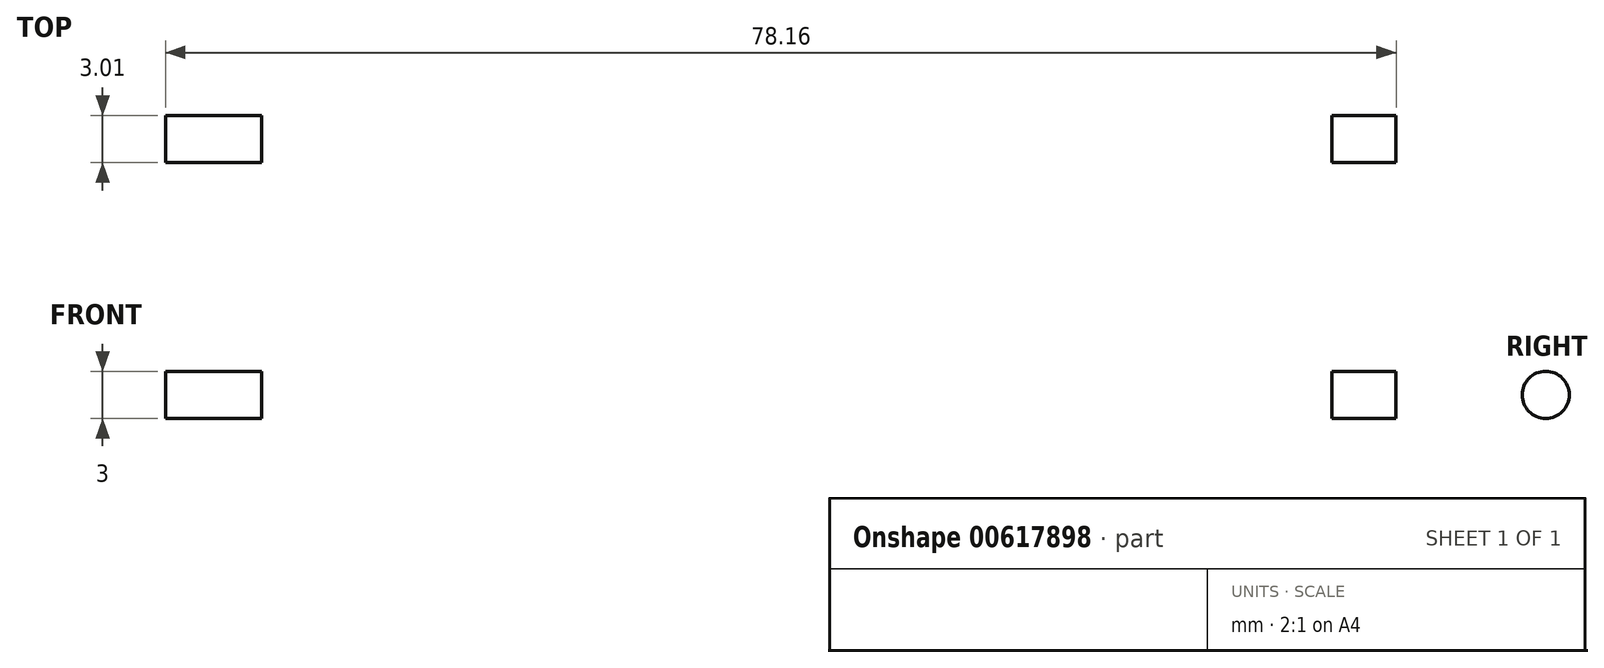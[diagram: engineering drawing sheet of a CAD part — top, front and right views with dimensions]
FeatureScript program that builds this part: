
annotation { "Feature Type Name" : "Feature", "Feature Type Description" : "" }
export const myFeature = defineFeature(function(context is Context, id is Id, definition is map)
    precondition{}
    {
        {
            var Q0;
            Q0=qCreatedBy(makeId("Front.planeOp"),FACE);
            var sketch = newSketch(context, id + "F0", { "sketchPlane" : qUnion([Q0])});
            skLineSegment(sketch, "E0.bottom", {"start": v(-39.07, 21.55) * mm, "end": v(39.08, 21.55) * mm});
            skLineSegment(sketch, "E0.top", {"start": v(-39.08, -21.55) * mm, "end": v(39.08, -21.55) * mm});
            skLineSegment(sketch, "E0.left", {"start": v(-39.07, 21.55) * mm, "end": v(-39.08, -21.55) * mm});
            skLineSegment(sketch, "E0.right", {"start": v(39.08, 21.55) * mm, "end": v(39.08, -21.55) * mm});
            skPoint(sketch, "E0.middle", {"position": v(0, 0) * mm});
            skSolve(sketch);
        }
        {
            var Q0;
            Q0=makeQuery(id+"F0.imprint","IMPRINT",FACE,{"disambiguationData":[TD([[makeQuery(id+"F0.imprint","IMPRINT",EDGE,{"derivedFrom":sQuery(id+"F0.wireOp",EDGE,"E0.bottom")}),-1.0]])]});
            extrude(context, id + "F1", {"entities" : qUnion([Q0]), "depth" : 19.23 * mm, "offsetDistance" : 25 * mm});
        }
        {
            var Q0;
            Q0=makeQuery(id+"F1.opExtrude","CAP_FACE",FACE,{"disambiguationData":[OSD([sQuery(id+"F0.wireOp",EDGE,"E0.bottom"),sQuery(id+"F0.wireOp",EDGE,"E0.top"),sQuery(id+"F0.wireOp",EDGE,"E0.left"),sQuery(id+"F0.wireOp",EDGE,"E0.right")])],"isStart":false});
            var sketch = newSketch(context, id + "F2", { "sketchPlane" : qUnion([Q0])});
            skLineSegment(sketch, "E1.bottom", {"start": v(-32.99, 18.42) * mm, "end": v(32.98, 18.42) * mm});
            skLineSegment(sketch, "E1.top", {"start": v(-32.98, -18.42) * mm, "end": v(32.99, -18.42) * mm});
            skLineSegment(sketch, "E1.left", {"start": v(-32.98, 18.42) * mm, "end": v(-32.98, -18.42) * mm});
            skLineSegment(sketch, "E1.right", {"start": v(32.99, 18.42) * mm, "end": v(32.99, -18.42) * mm});
            skPoint(sketch, "E1.middle", {"position": v(0, 0) * mm});
            skSolve(sketch);
        }
        {
            var Q0;
            Q0=makeQuery(id+"F2.imprint","IMPRINT",FACE,{"disambiguationData":[TD([[makeQuery(id+"F2.imprint","IMPRINT",EDGE,{"derivedFrom":sQuery(id+"F2.wireOp",EDGE,"E1.bottom")}),-1.0]])]});
            extrude(context, id + "F3", {"entities" : qUnion([Q0]), "operationType" : NewBodyOperationType.REMOVE, "oppositeDirection" : true, "depth" : 35 * mm, "offsetDistance" : 25 * mm});
        }
        {
            var Q0;
            Q0=makeQuery(id+"F1.opExtrude","SWEPT_FACE",FACE,{"disambiguationData":[OSD([sQuery(id+"F0.wireOp",EDGE,"E0.right")])]});
            var sketch = newSketch(context, id + "F4", { "sketchPlane" : qUnion([Q0])});
            skCircle(sketch, "E2", {"center": v(-9.62, 10.38) * mm, "radius": 1.5 * mm});
            skCircle(sketch, "E3.MirrorC", {"center": v(-9.62, -10.38) * mm, "radius": 1.5 * mm});
            skSolve(sketch);
        }
        {
            var Q0;
            Q0=makeQuery(id+"F4.imprint","IMPRINT",FACE,{"disambiguationData":[TD([[makeQuery(id+"F4.imprint","IMPRINT",EDGE,{"derivedFrom":sQuery(id+"F4.wireOp",EDGE,"E3.MirrorC")}),-1.0]])]});
            var Q1;
            Q1=makeQuery(id+"F4.imprint","IMPRINT",FACE,{"disambiguationData":[TD([[makeQuery(id+"F4.imprint","IMPRINT",EDGE,{"derivedFrom":sQuery(id+"F4.wireOp",EDGE,"E2")}),1.0]])]});
            extrude(context, id + "F5", {"entities" : qUnion([Q0, Q1]), "operationType" : NewBodyOperationType.REMOVE, "oppositeDirection" : true, "depth" : 80 * mm, "offsetDistance" : 25 * mm});
        }
        {
            var Q0;
            Q0=makeQuery(id+"F3.boolean.opBoolean","COPY",FACE,{"derivedFrom":makeQuery(id+"F3.opExtrude","SWEPT_FACE",FACE,{"disambiguationData":[OSD([sQuery(id+"F2.wireOp",EDGE,"E1.left")])]})});
            var sketch = newSketch(context, id + "F6", { "sketchPlane" : qUnion([Q0])});
            skCircle(sketch, "E4.cCircle", {"center": v(-9.62, 10.38) * mm, "radius": 3.18 * mm, "construction": true});
            skLineSegment(sketch, "E4.0", {"start": v(-6.54, 9.6) * mm, "end": v(-8.76, 7.32) * mm});
            skLineSegment(sketch, "E4.1", {"start": v(-8.76, 7.32) * mm, "end": v(-11.84, 8.1) * mm});
            skLineSegment(sketch, "E4.2", {"start": v(-11.84, 8.1) * mm, "end": v(-12.7, 11.17) * mm});
            skLineSegment(sketch, "E4.3", {"start": v(-12.7, 11.17) * mm, "end": v(-10.47, 13.44) * mm});
            skLineSegment(sketch, "E4.4", {"start": v(-10.47, 13.44) * mm, "end": v(-7.4, 12.65) * mm});
            skLineSegment(sketch, "E4.5", {"start": v(-7.4, 12.65) * mm, "end": v(-6.54, 9.6) * mm});
            skLineSegment(sketch, "E5.MirrorCS", {"start": v(-6.54, -9.6) * mm, "end": v(-8.76, -7.32) * mm});
            skCircle(sketch, "E6.MirrorC", {"center": v(-9.62, -10.38) * mm, "radius": 3.18 * mm, "construction": true});
            skLineSegment(sketch, "E7.MirrorCS", {"start": v(-7.4, -12.65) * mm, "end": v(-6.54, -9.6) * mm});
            skLineSegment(sketch, "E8.MirrorCS", {"start": v(-10.47, -13.44) * mm, "end": v(-7.4, -12.65) * mm});
            skLineSegment(sketch, "E9.MirrorCS", {"start": v(-8.76, -7.32) * mm, "end": v(-11.84, -8.1) * mm});
            skLineSegment(sketch, "E10.MirrorCS", {"start": v(-12.7, -11.17) * mm, "end": v(-10.47, -13.44) * mm});
            skLineSegment(sketch, "E11.MirrorCS", {"start": v(-11.84, -8.1) * mm, "end": v(-12.7, -11.17) * mm});
            skSolve(sketch);
        }
        {
            var Q0;
            Q0=makeQuery(id+"F6.imprint","IMPRINT",FACE,{"disambiguationData":[TD([[makeQuery(id+"F6.imprint","IMPRINT",EDGE,{"derivedFrom":sQuery(id+"F6.wireOp",EDGE,"E4.0")}),-1.0]])]});
            var Q1;
            Q1=makeQuery(id+"F6.imprint","IMPRINT",FACE,{"disambiguationData":[TD([[makeQuery(id+"F6.imprint","IMPRINT",EDGE,{"derivedFrom":sQuery(id+"F6.wireOp",EDGE,"E5.MirrorCS")}),1.0]])]});
            extrude(context, id + "F7", {"entities" : qUnion([Q0, Q1]), "operationType" : NewBodyOperationType.REMOVE, "oppositeDirection" : true, "depth" : 2 * mm, "offsetDistance" : 25 * mm});
        }
        {
            var Q0;
            Q0=makeQuery(id+"F3.boolean.opBoolean","COPY",FACE,{"derivedFrom":makeQuery(id+"F3.opExtrude","SWEPT_FACE",FACE,{"disambiguationData":[OSD([sQuery(id+"F2.wireOp",EDGE,"E1.right")])]})});
            var sketch = newSketch(context, id + "F8", { "sketchPlane" : qUnion([Q0])});
            skCircle(sketch, "E12.cCircle", {"center": v(9.62, 10.38) * mm, "radius": 3.18 * mm, "construction": true});
            skLineSegment(sketch, "E12.0", {"start": v(6.9, 12.03) * mm, "end": v(9.69, 13.55) * mm});
            skLineSegment(sketch, "E12.1", {"start": v(9.69, 13.55) * mm, "end": v(12.4, 11.9) * mm});
            skLineSegment(sketch, "E12.2", {"start": v(12.4, 11.9) * mm, "end": v(12.33, 8.73) * mm});
            skLineSegment(sketch, "E12.3", {"start": v(12.33, 8.73) * mm, "end": v(9.54, 7.2) * mm});
            skLineSegment(sketch, "E12.4", {"start": v(9.54, 7.2) * mm, "end": v(6.83, 8.85) * mm});
            skLineSegment(sketch, "E12.5", {"start": v(6.83, 8.85) * mm, "end": v(6.9, 12.03) * mm});
            skLineSegment(sketch, "E13.MirrorCS", {"start": v(9.69, -13.55) * mm, "end": v(12.4, -11.9) * mm});
            skLineSegment(sketch, "E14.MirrorCS", {"start": v(6.9, -12.03) * mm, "end": v(9.69, -13.55) * mm});
            skLineSegment(sketch, "E15.MirrorCS", {"start": v(6.83, -8.85) * mm, "end": v(6.9, -12.03) * mm});
            skLineSegment(sketch, "E16.MirrorCS", {"start": v(9.54, -7.2) * mm, "end": v(6.83, -8.85) * mm});
            skLineSegment(sketch, "E17.MirrorCS", {"start": v(12.33, -8.73) * mm, "end": v(9.54, -7.2) * mm});
            skLineSegment(sketch, "E18.MirrorCS", {"start": v(12.4, -11.9) * mm, "end": v(12.33, -8.73) * mm});
            skCircle(sketch, "E19.MirrorC", {"center": v(9.62, -10.38) * mm, "radius": 3.18 * mm, "construction": true});
            skSolve(sketch);
        }
        {
            var Q0;
            Q0 = qSketchRegion(id + "F8", true);
            extrude(context, id + "F9", {"entities" : qUnion([Q0]), "operationType" : NewBodyOperationType.REMOVE, "oppositeDirection" : true, "depth" : 2 * mm, "offsetDistance" : 25 * mm});
        }
    });
